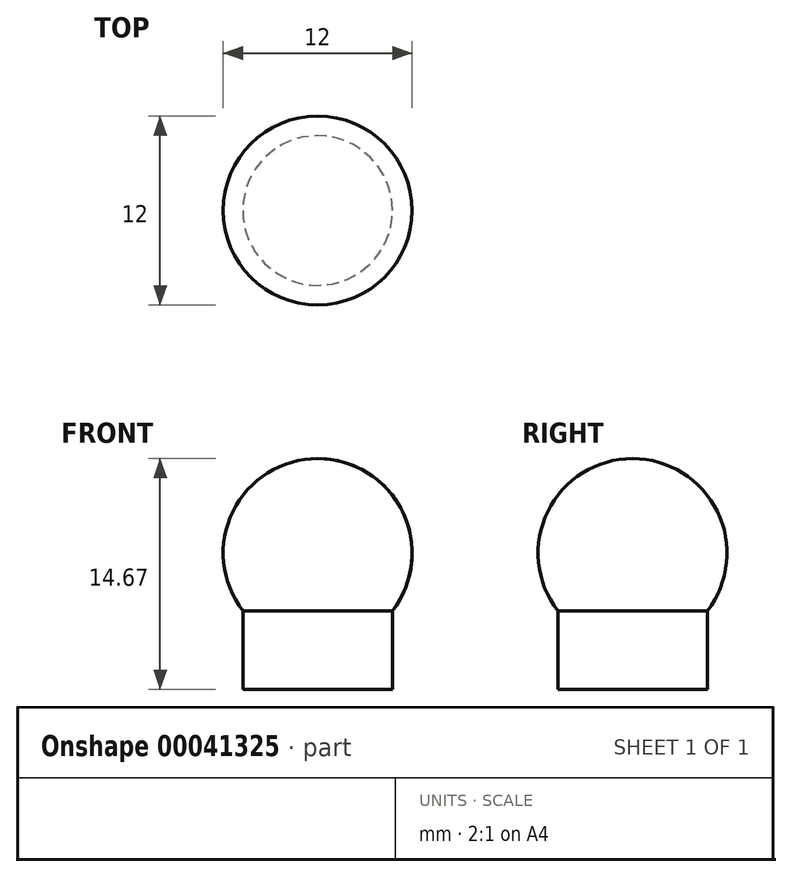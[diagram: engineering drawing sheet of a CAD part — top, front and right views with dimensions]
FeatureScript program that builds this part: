
annotation { "Feature Type Name" : "Feature", "Feature Type Description" : "" }
export const myFeature = defineFeature(function(context is Context, id is Id, definition is map)
    precondition{}
    {
        {
            var Q0;
            Q0=qCreatedBy(makeId("Front.planeOp"),FACE);
            var sketch = newSketch(context, id + "F0", { "sketchPlane" : qUnion([Q0])});
            skLineSegment(sketch, "E0.bottom", {"start": v(0, 0) * mm, "end": v(4.75, 0) * mm});
            skLineSegment(sketch, "E0.right", {"start": v(4.75, 0) * mm, "end": v(4.75, 5) * mm});
            skArc(sketch, "E1", {"start": v(4.75, 5) * mm, "mid": v(5.38, 11.31) * mm, "end": v(0, 14.67) * mm});
            skLineSegment(sketch, "E2", {"start": v(0, 0) * mm, "end": v(0, 14.67) * mm});
            skArc(sketch, "E3.MirrorCS", {"start": v(-4.75, 5) * mm, "mid": v(-5.38, 11.31) * mm, "end": v(0, 14.67) * mm, "construction": true});
            skLineSegment(sketch, "E4.MirrorCS", {"start": v(-4.75, 0) * mm, "end": v(-4.75, 5) * mm, "construction": true});
            skLineSegment(sketch, "E5.MirrorCS", {"start": v(0, 0) * mm, "end": v(-4.75, 0) * mm, "construction": true});
            skSolve(sketch);
        }
        {
            var Q0;
            Q0=makeQuery(id+"F0.imprint","IMPRINT",FACE,{"disambiguationData":[TD([[makeQuery(id+"F0.imprint","IMPRINT",EDGE,{"derivedFrom":sQuery(id+"F0.wireOp",EDGE,"E0.bottom")}),1.0]])]});
            var Q1;
            Q1=sQuery(id+"F0.wireOp",EDGE,"E2");
            revolve(context, id + "F1", {"entities" : qUnion([Q0]), "axis" : qUnion([Q1]), "revolveType" : RevolveType.FULL});
        }
    });
